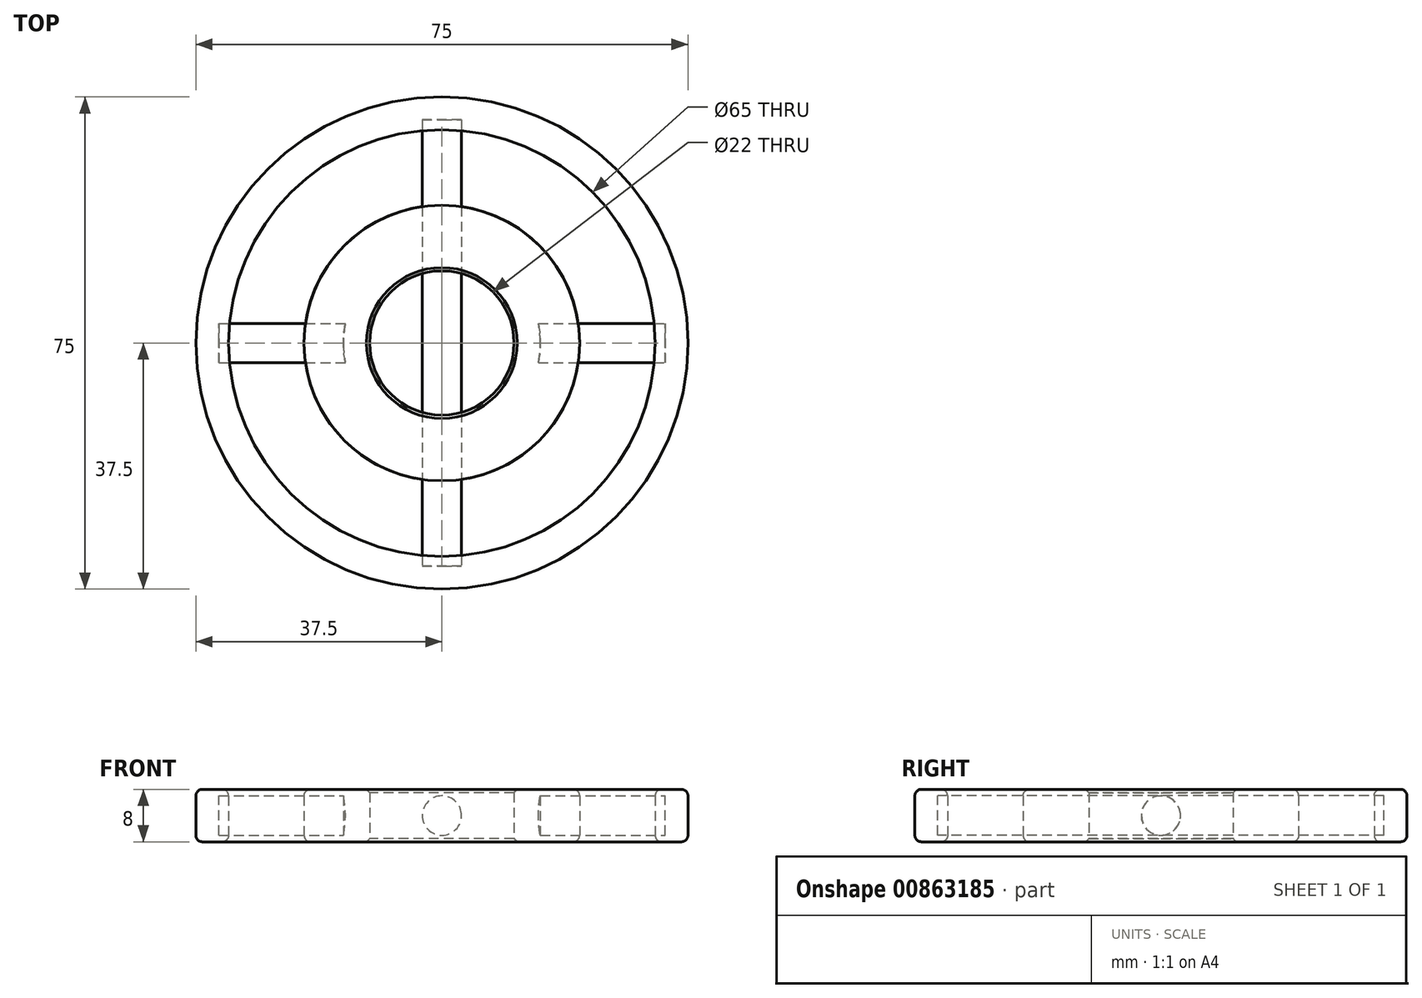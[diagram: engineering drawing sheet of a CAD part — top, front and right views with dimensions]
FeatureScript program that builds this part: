
annotation { "Feature Type Name" : "Feature", "Feature Type Description" : "" }
export const myFeature = defineFeature(function(context is Context, id is Id, definition is map)
    precondition{}
    {
        {
            var Q0;
            Q0=qCreatedBy(makeId("Top.planeOp"),FACE);
            var sketch = newSketch(context, id + "F0", { "sketchPlane" : qUnion([Q0])});
            skCircle(sketch, "E0", {"center": v(0, 0) * mm, "radius": 11 * mm});
            skCircle(sketch, "E1.0", {"center": v(0, 0) * mm, "radius": 21 * mm});
            skSolve(sketch);
        }
        {
            var Q0;
            Q0=qCreatedBy(makeId("Top.planeOp"),FACE);
            var sketch = newSketch(context, id + "F1", { "sketchPlane" : qUnion([Q0])});
            skCircle(sketch, "E2", {"center": v(0, 0) * mm, "radius": 32.5 * mm});
            skCircle(sketch, "E3.0", {"center": v(0, 0) * mm, "radius": 37.5 * mm});
            skSolve(sketch);
        }
        {
            var Q0;
            Q0 = qSketchRegion(id + "F0", true);
            extrude(context, id + "F2", {"entities" : qUnion([Q0]), "depth" : 8 * mm, "offsetDistance" : 25 * mm});
        }
        {
            var Q0;
            Q0 = qSketchRegion(id + "F1", true);
            extrude(context, id + "F3", {"entities" : qUnion([Q0]), "depth" : 8 * mm, "offsetDistance" : 25 * mm});
        }
        {
            var Q0;
            Q0=qCreatedBy(makeId("Front.planeOp"),FACE);
            var sketch = newSketch(context, id + "F4", { "sketchPlane" : qUnion([Q0])});
            skCircle(sketch, "E4", {"center": v(0, 4) * mm, "radius": 3 * mm});
            skSolve(sketch);
        }
        {
            var Q0;
            Q0=qCreatedBy(makeId("Top.planeOp"),FACE);
            var sketch = newSketch(context, id + "F5", { "sketchPlane" : qUnion([Q0])});
            skLineSegment(sketch, "E5", {"start": v(0, 34) * mm, "end": v(0, -34) * mm});
            skSolve(sketch);
        }
        {
            var Q0;
            Q0=makeQuery(id+"F4.imprint","IMPRINT",FACE,{"disambiguationData":[TD([[makeQuery(id+"F4.imprint","IMPRINT",EDGE,{"derivedFrom":sQuery(id+"F4.wireOp",EDGE,"E4")}),1.0]])]});
            var Q1;
            Q1 = qConstructionFilter(qBodyType(qCreatedBy(id + "F5" ,EDGE), BodyType.WIRE), ConstructionObject.NO);
            sweep(context, id + "F6", {"profiles" : qUnion([Q0]), "path" : qUnion([Q1])});
        }
        {
            var Q0;
            Q0=qCreatedBy(makeId("Right.planeOp"),FACE);
            var sketch = newSketch(context, id + "F7", { "sketchPlane" : qUnion([Q0])});
            skCircle(sketch, "E6", {"center": v(0, 4) * mm, "radius": 3 * mm});
            skSolve(sketch);
        }
        {
            var Q0;
            Q0=qCreatedBy(makeId("Top.planeOp"),FACE);
            var sketch = newSketch(context, id + "F8", { "sketchPlane" : qUnion([Q0])});
            skLineSegment(sketch, "E7", {"start": v(-34, 0) * mm, "end": v(34, 0) * mm});
            skSolve(sketch);
        }
        {
            var Q0;
            Q0 = qSketchRegion(id + "F7", true);
            var Q1;
            Q1 = qConstructionFilter(qBodyType(qCreatedBy(id + "F8" ,EDGE), BodyType.WIRE), ConstructionObject.NO);
            sweep(context, id + "F9", {"profiles" : qUnion([Q0]), "path" : qUnion([Q1])});
        }
        {
            var Q0;
            Q0=qCreatedBy(makeId("Top.planeOp"),FACE);
            var sketch = newSketch(context, id + "F10", { "sketchPlane" : qUnion([Q0])});
            skCircle(sketch, "E8", {"center": v(0, 0) * mm, "radius": 15 * mm});
            skSolve(sketch);
        }
        {
            var Q0;
            Q0 = qSketchRegion(id + "F10", true);
            var Q1;
            Q1=makeQuery(id+"F2.opExtrude","CAP_FACE",FACE,{"disambiguationData":[OSD([sQuery(id+"F0.wireOp",EDGE,"E0"),sQuery(id+"F0.wireOp",EDGE,"E1.0")])],"isStart":false});
            extrude(context, id + "F11", {"entities" : qUnion([Q0]), "endBound" : BoundingType.UP_TO_SURFACE, "depth" : 25 * mm, "endBoundEntityFace" : qUnion([Q1]), "offsetDistance" : 25 * mm});
        }
        {
            var Q0;
            Q0=makeQuery(id+"F11.opExtrude","SWEPT_BODY",BODY,{"disambiguationData":[OSD([sQuery(id+"F10.wireOp",EDGE,"E8")])]});
            var Q1;
            Q1=makeQuery(id+"F9.opSweep","SWEPT_BODY",BODY,{"disambiguationData":[OSD([sQuery(id+"F8.wireOp",EDGE,"E7"),sQuery(id+"F7.wireOp",EDGE,"E6")])]});
            booleanBodies(context, id + "F12", {"operationType" : BooleanOperationType.SUBTRACTION, "tools" : qUnion([Q0]), "targets" : qUnion([Q1])});
        }
        {
            var Q0;
            Q0=makeQuery(id+"F2.opExtrude","CAP_EDGE",EDGE,{"disambiguationData":[OSD([sQuery(id+"F0.wireOp",EDGE,"E0")])],"isStart":false});
            var Q1;
            Q1=makeQuery(id+"F2.opExtrude","CAP_EDGE",EDGE,{"disambiguationData":[OSD([sQuery(id+"F0.wireOp",EDGE,"E0")])],"isStart":true});
            chamfer(context, id + "F13", {"entities" : qUnion([Q0, Q1]), "width" : 0.5 * mm, "tangentPropagation" : true});
        }
        {
            var Q0;
            Q0=makeQuery(id+"F2.opExtrude","CAP_EDGE",EDGE,{"disambiguationData":[OSD([sQuery(id+"F0.wireOp",EDGE,"E1.0")])],"isStart":false});
            var Q1;
            Q1=makeQuery(id+"F2.opExtrude","CAP_EDGE",EDGE,{"disambiguationData":[OSD([sQuery(id+"F0.wireOp",EDGE,"E1.0")])],"isStart":true});
            var Q2;
            Q2=makeQuery(id+"F3.opExtrude","CAP_EDGE",EDGE,{"disambiguationData":[OSD([sQuery(id+"F1.wireOp",EDGE,"E2")])],"isStart":false});
            var Q3;
            Q3=makeQuery(id+"F3.opExtrude","CAP_EDGE",EDGE,{"disambiguationData":[OSD([sQuery(id+"F1.wireOp",EDGE,"E3.0")])],"isStart":false});
            var Q4;
            Q4=makeQuery(id+"F3.opExtrude","CAP_EDGE",EDGE,{"disambiguationData":[OSD([sQuery(id+"F1.wireOp",EDGE,"E3.0")])],"isStart":true});
            var Q5;
            Q5=makeQuery(id+"F3.opExtrude","CAP_EDGE",EDGE,{"disambiguationData":[OSD([sQuery(id+"F1.wireOp",EDGE,"E2")])],"isStart":true});
            fillet(context, id + "F14", {"entities" : qUnion([Q0, Q1, Q2, Q3, Q4, Q5]), "radius" : 1 * mm, "tangentPropagation" : true, "allowEdgeOverflow" : false});
        }
    });
